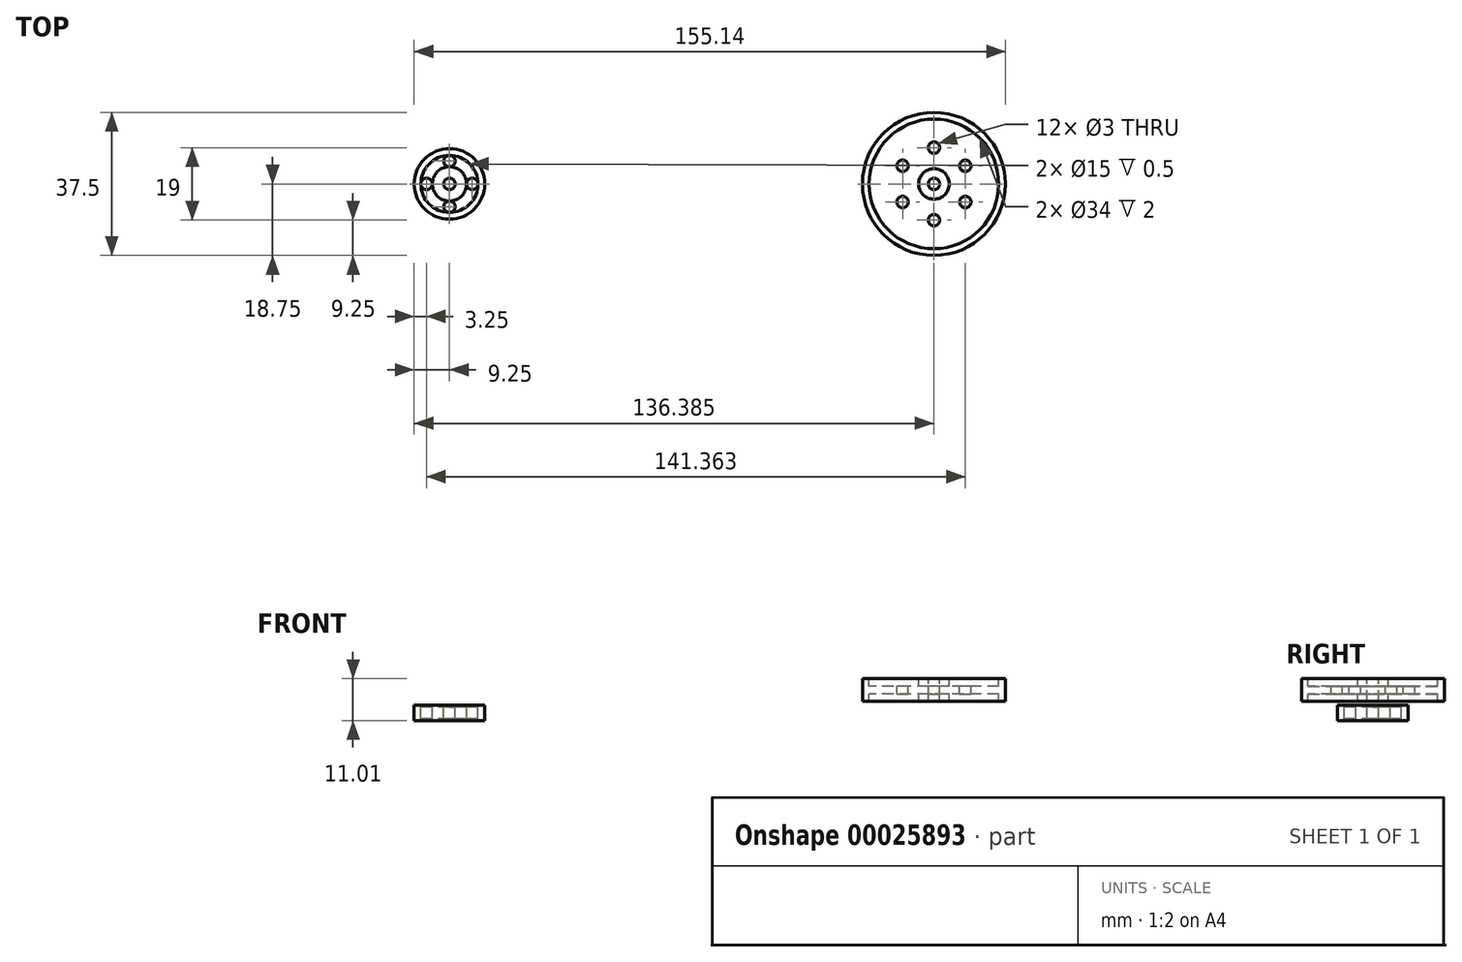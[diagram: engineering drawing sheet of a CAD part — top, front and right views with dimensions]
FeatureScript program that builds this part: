
annotation { "Feature Type Name" : "Feature", "Feature Type Description" : "" }
export const myFeature = defineFeature(function(context is Context, id is Id, definition is map)
    precondition{}
    {
        {
            var Q0;
            Q0=qCreatedBy(makeId("Front.planeOp"),FACE);
            var sketch = newSketch(context, id + "F0", { "sketchPlane" : qUnion([Q0])});
            skLineSegment(sketch, "E0", {"start": v(73.46, 9.8) * mm, "end": v(73.46, -11.85) * mm, "construction": true});
            skLineSegment(sketch, "E1.bottom", {"start": v(74.96, 1.32) * mm, "end": v(77.46, 1.32) * mm});
            skLineSegment(sketch, "E1.top", {"start": v(74.96, -4.68) * mm, "end": v(77.46, -4.68) * mm});
            skLineSegment(sketch, "E1.left", {"start": v(74.96, 1.32) * mm, "end": v(74.96, -4.68) * mm});
            skLineSegment(sketch, "E2", {"start": v(77.46, 1.32) * mm, "end": v(77.46, -0.68) * mm});
            skLineSegment(sketch, "E3", {"start": v(77.46, -0.68) * mm, "end": v(90.46, -0.68) * mm});
            skLineSegment(sketch, "E4", {"start": v(90.46, -0.68) * mm, "end": v(90.46, 1.32) * mm});
            skLineSegment(sketch, "E5", {"start": v(90.46, 1.32) * mm, "end": v(92.2, 1.32) * mm});
            skLineSegment(sketch, "E6", {"start": v(92.2, 1.32) * mm, "end": v(92.2, -4.68) * mm});
            skLineSegment(sketch, "E7", {"start": v(92.2, -4.68) * mm, "end": v(90.46, -4.68) * mm});
            skLineSegment(sketch, "E8", {"start": v(90.46, -4.68) * mm, "end": v(90.46, -2.68) * mm});
            skLineSegment(sketch, "E9", {"start": v(90.46, -2.68) * mm, "end": v(77.46, -2.68) * mm});
            skLineSegment(sketch, "E10", {"start": v(77.46, -2.68) * mm, "end": v(77.46, -4.68) * mm});
            skSolve(sketch);
        }
        {
            var Q0;
            Q0=makeQuery(id+"F0.imprint","IMPRINT",FACE,{"disambiguationData":[TD([[makeQuery(id+"F0.imprint","IMPRINT",EDGE,{"derivedFrom":sQuery(id+"F0.wireOp",EDGE,"E1.bottom")}),-1.0]])]});
            var Q1;
            Q1=sQuery(id+"F0.wireOp",EDGE,"E0");
            revolve(context, id + "F1", {"entities" : qUnion([Q0]), "axis" : qUnion([Q1]), "revolveType" : RevolveType.FULL});
        }
        {
            var Q0;
            Q0=makeQuery(id+"F1.opRevolve","SWEPT_FACE",FACE,{"disambiguationData":[OSD([sQuery(id+"F0.wireOp",EDGE,"E3")])]});
            var sketch = newSketch(context, id + "F2", { "sketchPlane" : qUnion([Q0])});
            skCircle(sketch, "E11.0", {"center": v(73.46, 0) * mm, "radius": 1.5 * mm});
            skCircle(sketch, "E12.1", {"center": v(73.46, 0) * mm, "radius": 4 * mm});
            skCircle(sketch, "E13.2", {"center": v(73.46, 0) * mm, "radius": 17 * mm});
            skCircle(sketch, "E14", {"center": v(73.46, 9.5) * mm, "radius": 1.5 * mm});
            skCircle(sketch, "E15.1.0", {"center": v(65.23, 4.75) * mm, "radius": 1.5 * mm});
            skCircle(sketch, "E15.2.0", {"center": v(65.23, -4.75) * mm, "radius": 1.5 * mm});
            skCircle(sketch, "E15.3.0", {"center": v(73.46, -9.5) * mm, "radius": 1.5 * mm});
            skCircle(sketch, "E15.4.0", {"center": v(81.68, -4.75) * mm, "radius": 1.5 * mm});
            skCircle(sketch, "E15.5.0", {"center": v(81.68, 4.75) * mm, "radius": 1.5 * mm});
            skSolve(sketch);
        }
        {
            var Q0;
            Q0=makeQuery(id+"F2.imprint","IMPRINT",FACE,{"disambiguationData":[TD([[makeQuery(id+"F2.imprint","IMPRINT",EDGE,{"derivedFrom":sQuery(id+"F2.wireOp",EDGE,"E15.5.0")}),1.0]])]});
            var Q1;
            Q1=makeQuery(id+"F2.imprint","IMPRINT",FACE,{"disambiguationData":[TD([[makeQuery(id+"F2.imprint","IMPRINT",EDGE,{"derivedFrom":sQuery(id+"F2.wireOp",EDGE,"E15.4.0")}),1.0]])]});
            var Q2;
            Q2=makeQuery(id+"F2.imprint","IMPRINT",FACE,{"disambiguationData":[TD([[makeQuery(id+"F2.imprint","IMPRINT",EDGE,{"derivedFrom":sQuery(id+"F2.wireOp",EDGE,"E15.3.0")}),1.0]])]});
            var Q3;
            Q3=makeQuery(id+"F2.imprint","IMPRINT",FACE,{"disambiguationData":[TD([[makeQuery(id+"F2.imprint","IMPRINT",EDGE,{"derivedFrom":sQuery(id+"F2.wireOp",EDGE,"E15.2.0")}),1.0]])]});
            var Q4;
            Q4=makeQuery(id+"F2.imprint","IMPRINT",FACE,{"disambiguationData":[TD([[makeQuery(id+"F2.imprint","IMPRINT",EDGE,{"derivedFrom":sQuery(id+"F2.wireOp",EDGE,"E15.1.0")}),1.0]])]});
            var Q5;
            Q5=makeQuery(id+"F2.imprint","IMPRINT",FACE,{"disambiguationData":[TD([[makeQuery(id+"F2.imprint","IMPRINT",EDGE,{"derivedFrom":sQuery(id+"F2.wireOp",EDGE,"E14")}),1.0]])]});
            extrude(context, id + "F3", {"entities" : qUnion([Q0, Q1, Q2, Q3, Q4, Q5]), "operationType" : NewBodyOperationType.REMOVE, "endBound" : BoundingType.THROUGH_ALL, "oppositeDirection" : true, "depth" : 25 * mm});
        }
        {
            var Q0;
            Q0=qCreatedBy(makeId("Front.planeOp"),FACE);
            var sketch = newSketch(context, id + "F4", { "sketchPlane" : qUnion([Q0])});
            skLineSegment(sketch, "E16", {"start": v(-53.68, 3.94) * mm, "end": v(-53.68, -18.56) * mm, "construction": true});
            skLineSegment(sketch, "E17.bottom", {"start": v(-52.18, -5.7) * mm, "end": v(-49.18, -5.7) * mm});
            skLineSegment(sketch, "E17.top", {"start": v(-52.18, -9.7) * mm, "end": v(-49.18, -9.7) * mm});
            skLineSegment(sketch, "E17.left", {"start": v(-52.18, -5.7) * mm, "end": v(-52.18, -9.7) * mm});
            skLineSegment(sketch, "E18", {"start": v(-49.18, -5.7) * mm, "end": v(-49.18, -6.2) * mm});
            skLineSegment(sketch, "E19", {"start": v(-49.18, -6.2) * mm, "end": v(-46.18, -6.2) * mm});
            skLineSegment(sketch, "E20", {"start": v(-46.18, -6.2) * mm, "end": v(-46.18, -5.7) * mm});
            skLineSegment(sketch, "E21", {"start": v(-46.18, -5.7) * mm, "end": v(-44.43, -5.7) * mm});
            skLineSegment(sketch, "E22", {"start": v(-44.43, -5.7) * mm, "end": v(-44.43, -9.7) * mm});
            skLineSegment(sketch, "E23", {"start": v(-44.43, -9.7) * mm, "end": v(-46.18, -9.7) * mm});
            skLineSegment(sketch, "E24", {"start": v(-46.18, -9.7) * mm, "end": v(-46.18, -9.2) * mm});
            skLineSegment(sketch, "E25", {"start": v(-46.18, -9.2) * mm, "end": v(-49.18, -9.2) * mm});
            skLineSegment(sketch, "E26", {"start": v(-49.18, -9.2) * mm, "end": v(-49.18, -9.7) * mm});
            skSolve(sketch);
        }
        {
            var Q0;
            Q0=makeQuery(id+"F4.imprint","IMPRINT",FACE,{"disambiguationData":[TD([[makeQuery(id+"F4.imprint","IMPRINT",EDGE,{"derivedFrom":sQuery(id+"F4.wireOp",EDGE,"E17.bottom")}),-1.0]])]});
            var Q1;
            Q1=sQuery(id+"F4.wireOp",EDGE,"E16");
            revolve(context, id + "F5", {"entities" : qUnion([Q0]), "axis" : qUnion([Q1]), "revolveType" : RevolveType.FULL});
        }
        {
            var Q0;
            Q0=makeQuery(id+"F5.opRevolve","SWEPT_FACE",FACE,{"disambiguationData":[OSD([sQuery(id+"F4.wireOp",EDGE,"E19")])]});
            var sketch = newSketch(context, id + "F6", { "sketchPlane" : qUnion([Q0])});
            skCircle(sketch, "E27.0", {"center": v(-53.68, 0) * mm, "radius": 1.5 * mm});
            skCircle(sketch, "E28.1", {"center": v(-53.68, 0) * mm, "radius": 4.5 * mm});
            skCircle(sketch, "E29.2", {"center": v(-53.68, 0) * mm, "radius": 7.5 * mm});
            skCircle(sketch, "E30", {"center": v(-53.68, 6) * mm, "radius": 1.5 * mm});
            skCircle(sketch, "E31.1.0", {"center": v(-59.68, 0) * mm, "radius": 1.5 * mm});
            skCircle(sketch, "E31.2.0", {"center": v(-53.68, -6) * mm, "radius": 1.5 * mm});
            skCircle(sketch, "E31.3.0", {"center": v(-47.68, 0) * mm, "radius": 1.5 * mm});
            skSolve(sketch);
        }
        {
            var Q0;
            {var subQ0=sQuery(id+"F6.wireOp",EDGE,"E31.1.0");var subQ2=makeQuery(id+"F6.imprint","INTERSECT",VERTEX,{"derivedFrom":[sQuery(id+"F6.wireOp",EDGE,"E29.2"),subQ0]});Q0=makeQuery(id+"F6.imprint","IMPRINT",FACE,{"disambiguationData":[TD([[makeQuery(id+"F6.imprint","IMPRINT",EDGE,{"disambiguationData":[TD([[subQ2,-1.0]])],"derivedFrom":subQ0}),1.0]])]});}
            var Q1;
            {var subQ0=sQuery(id+"F6.wireOp",EDGE,"E30");var subQ2=makeQuery(id+"F6.imprint","INTERSECT",VERTEX,{"derivedFrom":[sQuery(id+"F6.wireOp",EDGE,"E29.2"),subQ0]});Q1=makeQuery(id+"F6.imprint","IMPRINT",FACE,{"disambiguationData":[TD([[makeQuery(id+"F6.imprint","IMPRINT",EDGE,{"disambiguationData":[TD([[subQ2,-1.0]])],"derivedFrom":subQ0}),1.0]])]});}
            var Q2;
            {var subQ0=sQuery(id+"F6.wireOp",EDGE,"E31.3.0");var subQ2=makeQuery(id+"F6.imprint","INTERSECT",VERTEX,{"derivedFrom":[sQuery(id+"F6.wireOp",EDGE,"E29.2"),subQ0]});Q2=makeQuery(id+"F6.imprint","IMPRINT",FACE,{"disambiguationData":[TD([[makeQuery(id+"F6.imprint","IMPRINT",EDGE,{"disambiguationData":[TD([[subQ2,-1.0]])],"derivedFrom":subQ0}),1.0]])]});}
            var Q3;
            {var subQ0=sQuery(id+"F6.wireOp",EDGE,"E31.2.0");var subQ2=makeQuery(id+"F6.imprint","INTERSECT",VERTEX,{"derivedFrom":[sQuery(id+"F6.wireOp",EDGE,"E29.2"),subQ0]});Q3=makeQuery(id+"F6.imprint","IMPRINT",FACE,{"disambiguationData":[TD([[makeQuery(id+"F6.imprint","IMPRINT",EDGE,{"disambiguationData":[TD([[subQ2,-1.0]])],"derivedFrom":subQ0}),1.0]])]});}
            extrude(context, id + "F7", {"entities" : qUnion([Q0, Q1, Q2, Q3]), "operationType" : NewBodyOperationType.REMOVE, "endBound" : BoundingType.THROUGH_ALL, "oppositeDirection" : true, "depth" : 25 * mm});
        }
    });
